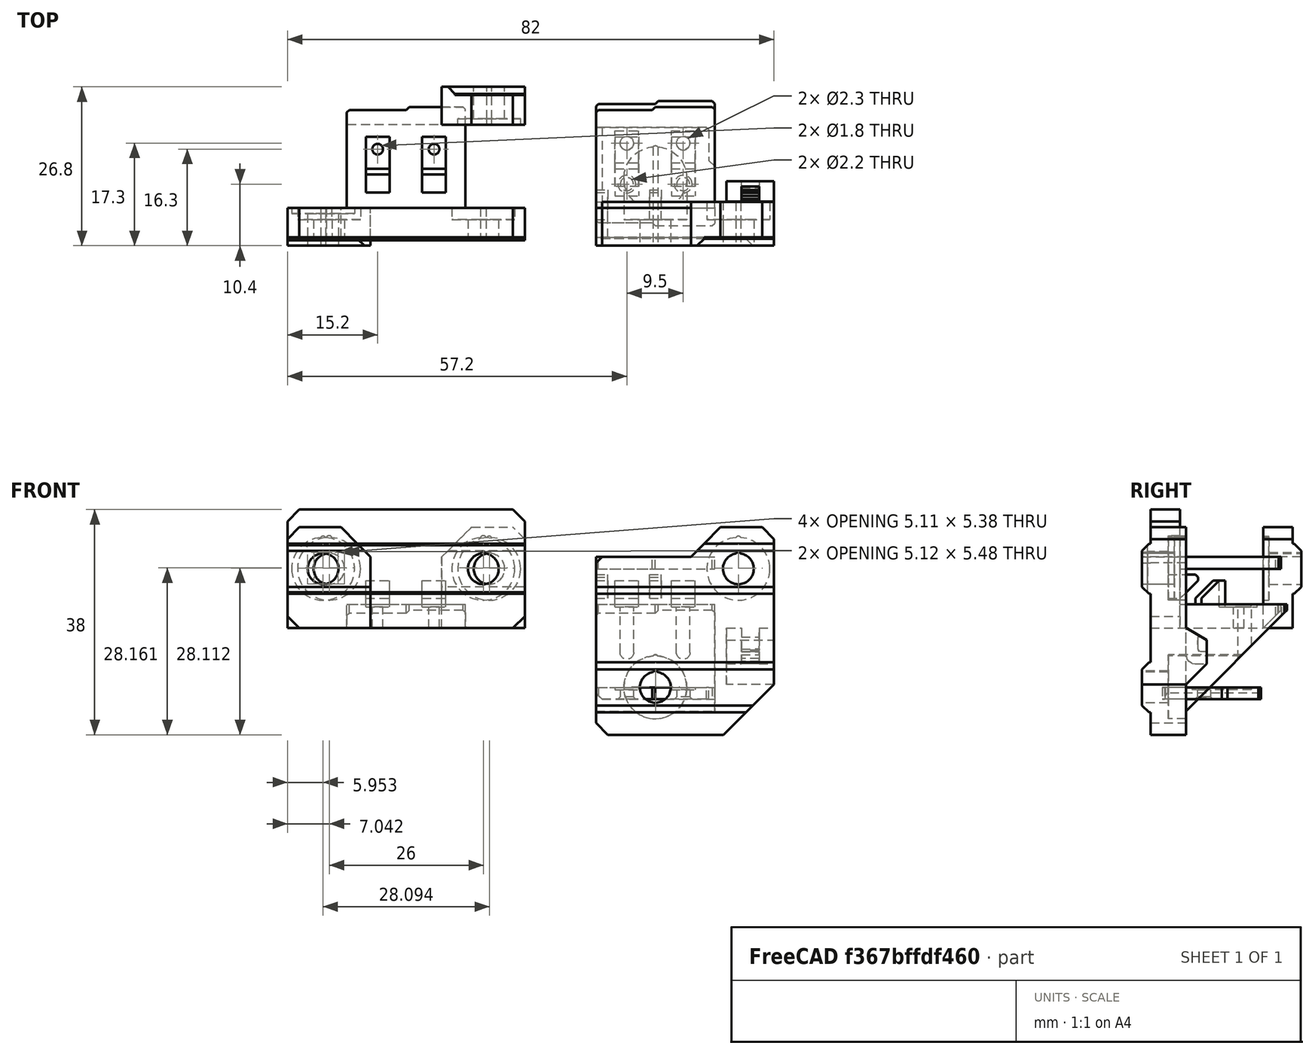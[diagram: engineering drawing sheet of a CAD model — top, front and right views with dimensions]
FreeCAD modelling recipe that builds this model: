
FCSTD DOCUMENT  (FreeCAD 0.18R14555 (Git shallow))
Label: Y-end-stop
License: All rights reserved
LicenseURL: http://en.wikipedia.org/wiki/All_rights_reserved
objects: Part::Cylinder×20, Part::Box×20, Part::MultiFuse×20, Part::Chamfer×18, Part::Cut×18, Part::Feature×17, Part::MultiCommon×3, Part::Mirroring×1
note: 117 computed .brp shape members not serialized (recipe doc carries the construction recipe); baked Part::Feature solids carry a one-line shape summary decoded from their .brp

FEATURE [Part::Cylinder] Cylinder
  Angle = 360
  AttacherType = Attacher::AttachEngine3D
  Height = 10
  Placement = pos=(5.2,2.9,0) rot=(0,0,1;0rad)
  Radius = 0.9
FEATURE [Part::Cylinder] Cylinder001
  Angle = 360
  AttacherType = Attacher::AttachEngine3D
  Height = 10
  Placement = pos=(14.7,2.9,0) rot=(0,0,1;0rad)
  Radius = 0.9
FEATURE [Part::Box] Box  label="Cube"
  AttacherType = Attacher::AttachEngine3D
  Height = 18
  Length = 10
  Placement = pos=(0,-7,-14) rot=(0,0,1;0rad)
  Width = 16.5
FEATURE [Part::Box] Box001  label="Cube001"
  AttacherType = Attacher::AttachEngine3D
  Height = 18
  Length = 10.5
  Placement = pos=(9.5,-7,-14) rot=(0,0,1;0rad)
  Width = 17
FEATURE [Part::Box] Box002  label="Cube002"
  AttacherType = Attacher::AttachEngine3D
  Height = 0.4
  Length = 4
  Placement = pos=(3.2,-0.4,3.6) rot=(0,0,1;0rad)
  Width = 5.4
FEATURE [Part::Box] Box003  label="Cube003"
  AttacherType = Attacher::AttachEngine3D
  Height = 0.4
  Length = 4
  Placement = pos=(12.7,-0.4,3.6) rot=(0,0,1;0rad)
  Width = 5.4
FEATURE [Part::Box] Box007  label="Cube007"
  AttacherType = Attacher::AttachEngine3D
  Height = 35
  Length = 30
  Placement = pos=(0,-12,-18) rot=(0,0,1;0rad)
  Width = 6
FEATURE [Part::MultiFuse] Fusion003
  Shapes = -> [Box003,Box002]
FEATURE [Part::Cylinder] Cylinder002
  Angle = 360
  AttacherType = Attacher::AttachEngine3D
  Height = 16
  Placement = pos=(10,9,-10) rot=(1,0,0;1.5708rad)
  Radius = 5.3
FEATURE [Part::Chamfer] Chamfer
  Base = -> Box001
  Edges = 1 edges r=1: [Edge3]
FEATURE [Part::Chamfer] Chamfer003
  Base = -> Box
  Edges = 1 edges r=0.4: [Edge3]
FEATURE [Part::Chamfer] Chamfer004
  Base = -> Chamfer
  Edges = 1 edges r=0.4: [Edge15]
FEATURE [Part::MultiFuse] Fusion
  Shapes = -> [Chamfer004,Chamfer003]
FEATURE [Part::Cut] Cut
  Base = -> Fusion
  Tool = -> Fusion003
FEATURE [Part::Feature] Body001
  Placement = pos=(0,-7,5) rot=(0,0,1;0rad)
  shape: bbox 20 x 19 x 19 mm, 5 faces (baked)
FEATURE [Part::Feature] Part__Feature  label="Common002"
  Placement = pos=(44.5,56.745,-30) rot=(0,0,1;3.14159rad)
  shape: bbox 8 x 3.5 x 9.5 mm, 30 faces (baked)
FEATURE [Part::Cylinder] Cylinder004
  Angle = 360
  AttacherType = Attacher::AttachEngine3D
  Height = 16
  Placement = pos=(24,9,10) rot=(1,0,0;1.5708rad)
  Radius = 5.3
FEATURE [Part::Feature] Fusion008001  label="Fusion009"
  shape: bbox 30 x 1.4 x 8.45 mm, 8 faces (baked)
FEATURE [Part::Feature] Fusion008002  label="Fusion010"
  Placement = pos=(0,0,20) rot=(0,0,1;0rad)
  shape: bbox 30 x 1.4 x 8.45 mm, 8 faces (baked)
FEATURE [Part::MultiFuse] Fusion008005
  Placement = pos=(0,0,-5) rot=(0,0,1;0rad)
  Shapes = -> [Cylinder001,Cylinder]
FEATURE [Part::Cylinder] Cylinder005
  Angle = 360
  AttacherType = Attacher::AttachEngine3D
  Height = 25
  Placement = pos=(24,9,10) rot=(1,0,0;1.5708rad)
  Radius = 2.6
FEATURE [Part::Cylinder] Cylinder006
  Angle = 360
  AttacherType = Attacher::AttachEngine3D
  Height = 25
  Placement = pos=(10,9,-10) rot=(1,0,0;1.5708rad)
  Radius = 2.6
FEATURE [Part::Cylinder] Cylinder007
  Angle = 360
  AttacherType = Attacher::AttachEngine3D
  Height = 25
  Placement = pos=(24,9,12.3) rot=(1,0,0;1.5708rad)
  Radius = 0.5
FEATURE [Part::Cylinder] Cylinder008
  Angle = 360
  AttacherType = Attacher::AttachEngine3D
  Height = 25
  Placement = pos=(10,9,-7.7) rot=(1,0,0;1.5708rad)
  Radius = 0.5
FEATURE [Part::MultiFuse] Fusion008010
  Shapes = -> [Cylinder005,Cylinder006]
FEATURE [Part::Cylinder] Cylinder009
  Angle = 360
  AttacherType = Attacher::AttachEngine3D
  Height = 16
  Placement = pos=(24,8,15) rot=(1,0,0;1.5708rad)
  Radius = 0.5
FEATURE [Part::Cylinder] Cylinder010
  Angle = 360
  AttacherType = Attacher::AttachEngine3D
  Height = 16
  Placement = pos=(10,8,-5) rot=(1,0,0;1.5708rad)
  Radius = 0.5
FEATURE [Part::MultiFuse] Fusion008011
  Placement = pos=(0,-1,0) rot=(0,0,1;0rad)
  Shapes = -> [Cylinder004,Cylinder002]
FEATURE [Part::Box] Box011  label="Cube011"
  AttacherType = Attacher::AttachEngine3D
  Height = 4
  Length = 2
  Placement = pos=(9,0,7) rot=(0,0,1;0rad)
  Width = 5
FEATURE [Part::Chamfer] Chamfer005
  Base = -> Box011
  Edges = 1 edges r=3: [Edge11]
  Placement = pos=(0,-9,-2) rot=(0,0,1;0rad)
FEATURE [Part::Chamfer] Chamfer006
  Base = -> Chamfer005
  Edges = 1 edges r=0.4: [Edge8]
FEATURE [Part::Feature] Chamfer006001  label="Chamfer007"
  shape: bbox 2 x 5 x 4 mm, 8 faces (baked)
FEATURE [Part::Feature] Chamfer006002  label="Chamfer008"
  Placement = pos=(-9,0,0) rot=(0,0,1;0rad)
  shape: bbox 2 x 5 x 4 mm, 8 faces (baked)
FEATURE [Part::Feature] Chamfer002001  label="Chamfer009"
  Placement = pos=(0,1,-2) rot=(0,0,1;0rad)
  shape: bbox 4 x 4 x 6 mm, 7 faces (baked)
FEATURE [Part::Feature] Chamfer001001  label="Chamfer010"
  Placement = pos=(0,1,-2) rot=(0,0,1;0rad)
  shape: bbox 4 x 4 x 6 mm, 7 faces (baked)
FEATURE [Part::Cut] Cut001
  Base = -> Cut
  Tool = -> Body001
FEATURE [Part::Cut] Cut002
  Base = -> Cut001
  Placement = pos=(0,1,0) rot=(0,0,1;0rad)
  Tool = -> Fusion008005
FEATURE [Part::MultiFuse] Fusion008012
  Shapes = -> [Fusion008010,Cylinder008]
FEATURE [Part::MultiFuse] Fusion008013
  Shapes = -> [Fusion008011,Cylinder010]
FEATURE [Part::MultiFuse] Fusion008014
  Shapes = -> [Fusion008012,Cylinder007]
FEATURE [Part::MultiFuse] Fusion008015
  Placement = pos=(0,-1,0) rot=(0,0,1;0rad)
  Shapes = -> [Fusion008013,Cylinder009]
FEATURE [Part::Box] Box012  label="Cube012"
  AttacherType = Attacher::AttachEngine3D
  Height = 10
  Length = 22
  Width = 10
FEATURE [Part::Box] Box013  label="Cube013"
  AttacherType = Attacher::AttachEngine3D
  Height = 14
  Length = 14
  Placement = pos=(28,-15,-29) rot=(0,0,1;0rad)
  Width = 14
FEATURE [Part::Chamfer] Chamfer006004
  Base = -> Box013
  Edges = 1 edges r=9: [Edge2]
  Placement = pos=(-7,0,5.5) rot=(0,0,1;0rad)
FEATURE [Part::Box] Box014  label="Cube014"
  AttacherType = Attacher::AttachEngine3D
  Height = 2
  Length = 10
  Placement = pos=(0,-7,10) rot=(0,0,1;0rad)
  Width = 16.5
FEATURE [Part::Box] Box015  label="Cube015"
  AttacherType = Attacher::AttachEngine3D
  Height = 2
  Length = 11
  Placement = pos=(9,-7,10) rot=(0,0,1;0rad)
  Width = 17
FEATURE [Part::Chamfer] Chamfer006009
  Base = -> Box014
  Edges = 1 edges r=0.4: [Edge3]
FEATURE [Part::Chamfer] Chamfer006010
  Base = -> Box015
  Edges = 1 edges r=1: [Edge3]
FEATURE [Part::Chamfer] Chamfer006011
  Base = -> Chamfer006010
  Edges = 1 edges r=0.4: [Edge15]
FEATURE [Part::MultiFuse] Fusion008018
  Shapes = -> [Chamfer006009,Chamfer006011]
FEATURE [Part::Feature] Fusion008018001  label="Fusion008019"
  shape: bbox 20 x 17 x 2 mm, 10 faces (baked)
FEATURE [Part::Box] Box016  label="Cube016"
  AttacherType = Attacher::AttachEngine3D
  Height = 0.4
  Length = 4
  Placement = pos=(3.2,0,0) rot=(0,0,1;0rad)
  Width = 10
FEATURE [Part::Box] Box017  label="Cube017"
  AttacherType = Attacher::AttachEngine3D
  Height = 0.4
  Length = 4
  Placement = pos=(12.7,0,0) rot=(0,0,1;0rad)
  Width = 10
FEATURE [Part::MultiFuse] Fusion008018002
  Placement = pos=(0,-5,10) rot=(0,0,1;0rad)
  Shapes = -> [Box017,Box016]
FEATURE [Part::Cut] Cut007
  Base = -> Fusion008018001
  Tool = -> Fusion008018002
FEATURE [Part::Cylinder] Cylinder011
  Angle = 360
  AttacherType = Attacher::AttachEngine3D
  Height = 10
  Placement = pos=(5.2,3,0) rot=(0,0,1;0rad)
  Radius = 1.1
FEATURE [Part::Cylinder] Cylinder012
  Angle = 360
  AttacherType = Attacher::AttachEngine3D
  Height = 10
  Placement = pos=(14.7,3,0) rot=(0,0,1;0rad)
  Radius = 1.1
FEATURE [Part::MultiFuse] Fusion008018003
  Placement = pos=(0,0,5) rot=(0,0,1;0rad)
  Shapes = -> [Cylinder011,Cylinder012]
FEATURE [Part::Cut] Cut008
  Base = -> Cut007
  Tool = -> Fusion008018003
FEATURE [Part::Chamfer] Chamfer006012
  Base = -> Cut008
  Edges = 2 edges r=0.4: [Edge12,Edge13]
FEATURE [Part::Box] Box018  label="Cube018"
  AttacherType = Attacher::AttachEngine3D
  Height = 10
  Length = 20
  Placement = pos=(0,-16.6,7) rot=(0,0,1;0rad)
  Width = 10
FEATURE [Part::Cut] Cut009  label="lit"
  Base = -> Chamfer006012
  Tool = -> Box018
FEATURE [Part::Chamfer] Chamfer006013
  Base = -> Box012
  Edges = 1 edges r=5: [Edge8]
  Placement = pos=(-1,-14,12) rot=(0,0,1;0rad)
FEATURE [Part::Box] Box019  label="Cube019"
  AttacherType = Attacher::AttachEngine3D
  Height = 10
  Length = 10
  Placement = pos=(0,-15,14) rot=(0,0,1;0rad)
  Width = 10
FEATURE [Part::Chamfer] Chamfer006015
  Base = -> Box019
  Edges = 1 edges r=3: [Edge8]
  Placement = pos=(-8,0,-4) rot=(0,0,1;0rad)
FEATURE [Part::Chamfer] Chamfer006016
  Base = -> Cut009
  Edges = 1 edges r=1: [Edge8]
FEATURE [Part::Box] Box021  label="Cube021"
  AttacherType = Attacher::AttachEngine3D
  Height = 10
  Length = 10
  Placement = pos=(19,-13,2) rot=(0,0,1;0rad)
  Width = 10
FEATURE [Part::Chamfer] Chamfer006020
  Base = -> Box021
  Edges = 1 edges r=1: [Edge3]
  Placement = pos=(0,3,0) rot=(0,0,1;0rad)
FEATURE [Part::Cut] Cut013
  Base = -> Chamfer006016
  Tool = -> Chamfer006020
FEATURE [Part::Chamfer] Chamfer006021
  Base = -> Cut013
  Edges = 1 edges r=0.4: [Edge27]
  Placement = pos=(0,0,0) rot=(1,0,0;3.14159rad)
FEATURE [Part::Feature] Chamfer006019001  label="Chamfer006022"
  shape: bbox 30 x 23.4 x 35 mm, 92 faces (baked)
FEATURE [Part::Box] Box022  label="Cube022"
  AttacherType = Attacher::AttachEngine3D
  Height = 20
  Length = 37
  Placement = pos=(0,-15,0) rot=(0,0,1;0rad)
  Width = 26
FEATURE [Part::MultiCommon] Common
  Placement = pos=(-42,0,0) rot=(0,0,1;0rad)
  Shapes = -> [Box022,Chamfer006019001]
FEATURE [Part::Box] Box023  label="Cube023"
  AttacherType = Attacher::AttachEngine3D
  Height = 19
  Length = 17
  Placement = pos=(-26,-17,0) rot=(0,0,1;0rad)
  Width = 10
FEATURE [Part::Feature] Common001  label="Common003"
  Placement = pos=(-42,0,0) rot=(0,0,1;0rad)
  shape: bbox 30 x 23.4 x 17 mm, 51 faces (baked)
FEATURE [Part::MultiCommon] Common002  label="Common004"
  Shapes = -> [Box023,Common001]
FEATURE [Part::Mirroring] Part__Mirroring  label="Common004 (Mirror #1)"
  Base = (0,0,0)
  Normal = (0,1,0)
  Source = -> Common002
FEATURE [Part::Feature] Part__Mirroring001  label="Common004 (Mirror #1)001"
  Placement = pos=(-64,8e-15,0) rot=(0,0,1;3.14159rad)
  shape: bbox 14 x 6.4 x 17 mm, 20 faces (baked)
FEATURE [Part::Chamfer] Chamfer006019002
  Base = -> Common
  Edges = 1 edges r=3: [Edge69]
FEATURE [Part::Box] Box024  label="Cube024"
  AttacherType = Attacher::AttachEngine3D
  Height = 18
  Length = 23
  Placement = pos=(-43,-7,0) rot=(0,0,1;0rad)
  Width = 21
FEATURE [Part::MultiCommon] Common003  label="Common005"
  Shapes = -> [Chamfer006019002,Box024]
FEATURE [Part::Box] Box025  label="Cube025"
  AttacherType = Attacher::AttachEngine3D
  Height = 20
  Length = 40
  Placement = pos=(-52,-12,0) rot=(0,0,1;0rad)
  Width = 5
FEATURE [Part::Cylinder] Cylinder013
  Angle = 360
  AttacherType = Attacher::AttachEngine3D
  Height = 2
  Placement = pos=(-45,-7,10) rot=(1,0,0;1.5708rad)
  Radius = 5.3
FEATURE [Part::Cylinder] Cylinder014
  Angle = 360
  AttacherType = Attacher::AttachEngine3D
  Height = 2
  Placement = pos=(-19,-7,10) rot=(1,0,0;1.5708rad)
  Radius = 5.3
FEATURE [Part::Feature] Part__Feature001  label="v-slot-stablizer"
  Placement = pos=(-26,-12,21.005) rot=(0.57735,-0.57735,-0.57735;4.18879rad)
  shape: bbox 10 x 1.4 x 8.45 mm, 8 faces (baked)
FEATURE [Part::Feature] Part__Feature002  label="v-slot-stablizer001"
  Placement = pos=(-16,-12,21.005) rot=(0.57735,-0.57735,-0.57735;4.18879rad)
  shape: bbox 10 x 1.4 x 8.45 mm, 8 faces (baked)
FEATURE [Part::Feature] Part__Feature003  label="v-slot-stablizer002"
  Placement = pos=(4,-12,21.005) rot=(0.57735,-0.57735,-0.57735;4.18879rad)
  shape: bbox 10 x 1.4 x 8.45 mm, 8 faces (baked)
FEATURE [Part::Feature] Part__Feature004  label="v-slot-stablizer003"
  Placement = pos=(-6,-12,21.005) rot=(0.57735,-0.57735,-0.57735;4.18879rad)
  shape: bbox 10 x 1.4 x 8.45 mm, 8 faces (baked)
FEATURE [Part::MultiFuse] Fusion008018005
  Shapes = -> [Part__Feature001,Part__Feature002,Part__Feature004,Part__Feature003]
FEATURE [Part::Box] Box026  label="Cube026"
  AttacherType = Attacher::AttachEngine3D
  Height = 20
  Length = 40
  Placement = pos=(-52,-17.5,0) rot=(0,0,1;0rad)
  Width = 5
FEATURE [Part::Cut] Cut014
  Base = -> Fusion008018005
  Tool = -> Box026
FEATURE [Part::Cylinder] Cylinder015
  Angle = 360
  AttacherType = Attacher::AttachEngine3D
  Height = 10
  Placement = pos=(-19,-6,12.4) rot=(1,0,0;1.5708rad)
  Radius = 0.5
FEATURE [Part::Cylinder] Cylinder016
  Angle = 360
  AttacherType = Attacher::AttachEngine3D
  Height = 10
  Placement = pos=(-45,-6,12.4) rot=(1,0,0;1.5708rad)
  Radius = 0.5
FEATURE [Part::MultiFuse] Fusion008018007
  Shapes = -> [Cut014,Box025]
FEATURE [Part::Feature] Fusion008018006001  label="Fusion008018008"
  shape: bbox 31.2 x 10 x 5.2 mm, 6 faces, 2 solids (baked)
FEATURE [Part::Cut] Cut015
  Base = -> Fusion008018007
  Tool = -> Fusion008018006001
FEATURE [Part::MultiFuse] Fusion008018006002
  Shapes = -> [Cylinder016,Cylinder015]
FEATURE [Part::Cut] Cut016
  Base = -> Cut015
  Tool = -> Fusion008018006002
FEATURE [Part::Cylinder] Cylinder017
  Angle = 360
  AttacherType = Attacher::AttachEngine3D
  Height = 2
  Placement = pos=(-19,-7,15.1) rot=(1,0,0;1.5708rad)
  Radius = 0.5
FEATURE [Part::Cylinder] Cylinder018
  Angle = 360
  AttacherType = Attacher::AttachEngine3D
  Height = 2
  Placement = pos=(-45,-7,15.1) rot=(1,0,0;1.5708rad)
  Radius = 0.5
FEATURE [Part::MultiFuse] Fusion008018006003
  Shapes = -> [Cylinder014,Cylinder013]
FEATURE [Part::Cut] Cut017
  Base = -> Cut016
  Tool = -> Fusion008018006003
FEATURE [Part::MultiFuse] Fusion008018006004
  Shapes = -> [Cylinder018,Cylinder017]
FEATURE [Part::Cut] Cut018
  Base = -> Cut017
  Tool = -> Fusion008018006004
FEATURE [Part::Chamfer] Chamfer006019003
  Base = -> Cut018
  Edges = 4 edges r=2: [Edge4,Edge6,Edge25,Edge34]
FEATURE [Part::MultiFuse] Fusion008018006005  label="slim"
  Shapes = -> [Chamfer006019003,Common003]
FEATURE [Part::MultiFuse] Fusion008018006006
  Shapes = -> [Box007,Fusion008001,Fusion008002,Part__Feature,Cut002,Chamfer001001,Chamfer002001]
FEATURE [Part::Cut] Cut019
  Base = -> Fusion008018006006
  Tool = -> Chamfer006004
FEATURE [Part::Cut] Cut020
  Base = -> Cut019
  Tool = -> Chamfer006013
FEATURE [Part::Cut] Cut021
  Base = -> Cut020
  Tool = -> Chamfer006015
FEATURE [Part::Cut] Cut022
  Base = -> Cut021
  Tool = -> Fusion008015
FEATURE [Part::Cut] Cut023
  Base = -> Cut022
  Tool = -> Fusion008014
FEATURE [Part::Chamfer] Chamfer006019004
  Base = -> Cut023
  Edges = 2 edges r=2: [Edge9,Edge75]
FEATURE [Part::Cylinder] Cylinder019
  Angle = 360
  AttacherType = Attacher::AttachEngine3D
  Height = 15
  Placement = pos=(5.2,3.9,-6) rot=(0,0,1;0rad)
  Radius = 1.15
FEATURE [Part::Cylinder] Cylinder020
  Angle = 360
  AttacherType = Attacher::AttachEngine3D
  Height = 15
  Placement = pos=(14.7,3.9,-6) rot=(0,0,1;0rad)
  Radius = 1.15
FEATURE [Part::MultiFuse] Fusion008018006007
  Placement = pos=(0,0,-1) rot=(0,0,1;0rad)
  Shapes = -> [Cylinder020,Cylinder019]
FEATURE [Part::Cut] Cut024
  Base = -> Chamfer006019004
  Tool = -> Fusion008018006007
